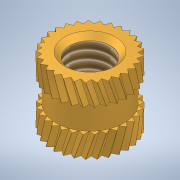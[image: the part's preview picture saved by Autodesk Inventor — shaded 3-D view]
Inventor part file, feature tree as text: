
AUTODESK INVENTOR PART (.ipt)
format: ipt  version: 2022 (Build 260153000, 153)  size: 768,512 bytes
history: native  units: mm
features: sketch x4, revolve x1, loft x1, pattern_circular x1, plane x1, mirror x1, hole x1, chamfer x1, projected_geometry x1
ambient origin geometry x8: Origin, YZ Plane, XZ Plane, XY Plane, X Axis, Y Axis, Z Axis, Center Point
bodies: Solid1 (feature_tree)
feature tree (12):
  revolve  "Revolution1"  [1 undecoded]
  loft  "Loft2"
  pattern_circular  "Circular Pattern2"  [2 undecoded]
  plane  "Work Plane1"
  mirror  "Mirror1"
  hole  "Hole1"  [1 undecoded]
  chamfer  "Chamfer1"  Distance=0.25mm
  sketch  "Sketch1"  dims[d0=2.3mm d1=4.0mm]
  sketch  "Sketch2"  dims[d2=0.25mm d3=1.3mm d4=1.3mm d5=1.3mm]
  projected_geometry  "Projected Loop1"
  sketch  "Sketch3"  dims[d6=90.0deg]
  sketch  "Sketch4"  dims[d16=0.5mm d17=0.25mm d18=0.5mm d19=0.25mm d20=0.0mm d21=90.0deg d22=0.0mm d23=90.0deg d24=0.1mm d25=0.1mm d26=1.745329mm d30=290.0mm d31=360.0deg d33=2.459mm d34=6.0mm d35=6.3mm d36=2.0mm d37=90.0deg d38=8.0mm d39=20.594885mm d40=0.3mm d41=2.0mm d42=45.0deg d43=0.25mm d44=0.25mm]
note: 4 required parameter values undecoded (feature->parameter linkage not recoverable at this tier; creation-order binding heuristic only, values carry confidence <= 0.55)